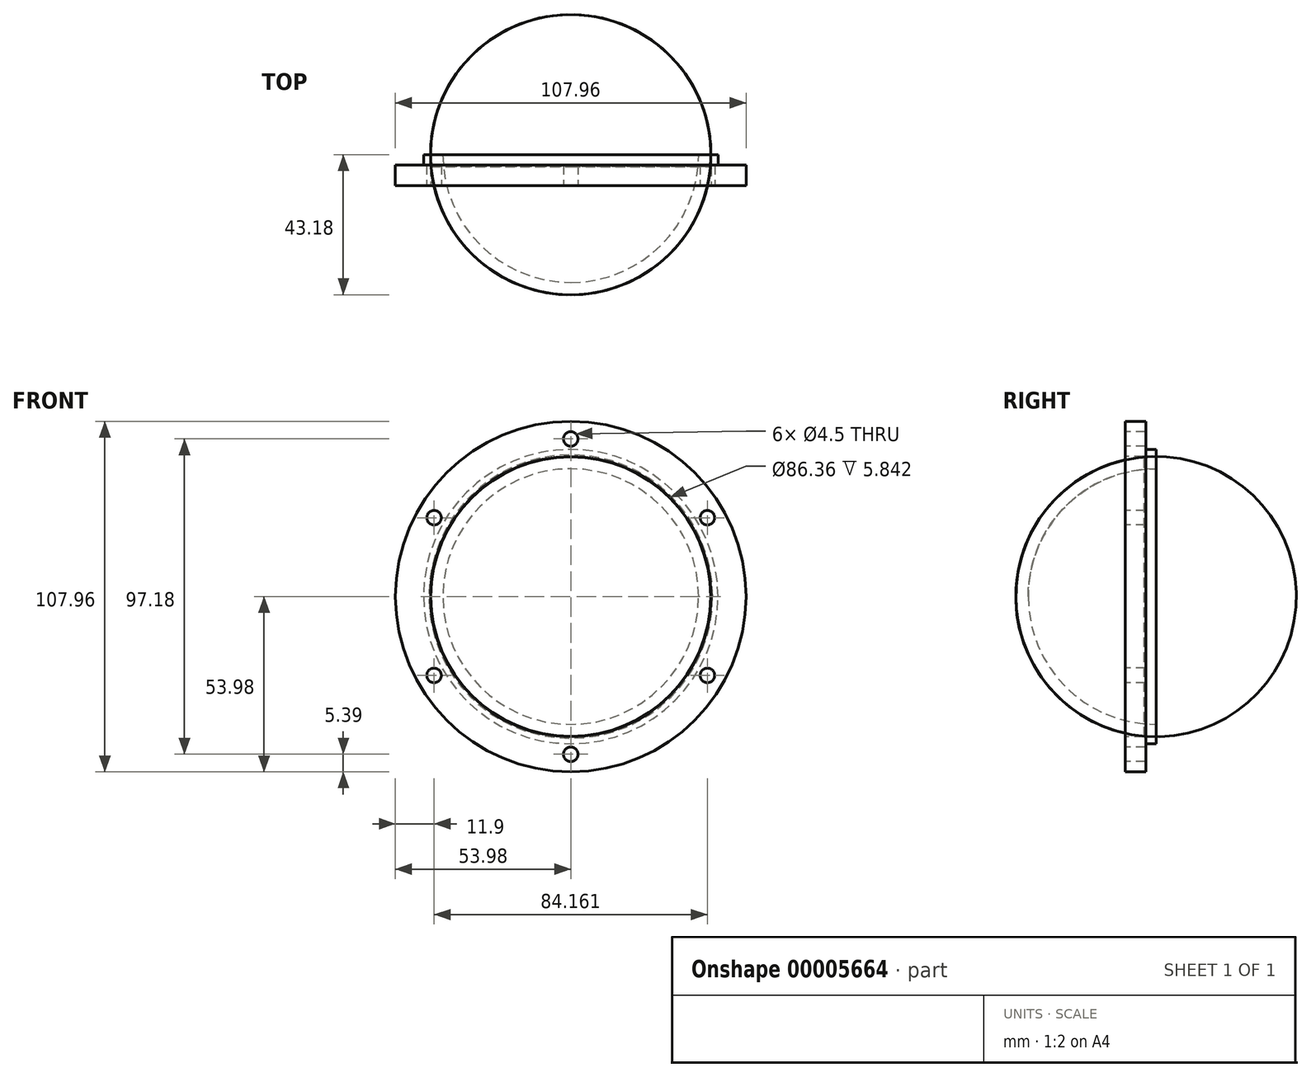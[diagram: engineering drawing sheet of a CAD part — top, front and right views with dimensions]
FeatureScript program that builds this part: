
annotation { "Feature Type Name" : "Feature", "Feature Type Description" : "" }
export const myFeature = defineFeature(function(context is Context, id is Id, definition is map)
    precondition{}
    {
        {
            var Q0;
            Q0=qCreatedBy(makeId("Right.planeOp"),FACE);
            var sketch = newSketch(context, id + "F0", { "sketchPlane" : qUnion([Q0])});
            skLineSegment(sketch, "E0", {"start": v(0, 0) * mm, "end": v(55.44, 0) * mm, "construction": true});
            skLineSegment(sketch, "E1", {"start": v(0, 43.18) * mm, "end": v(6.35, 43.18) * mm});
            skLineSegment(sketch, "E2", {"start": v(6.35, 43.18) * mm, "end": v(6.35, 43.18) * mm});
            skLineSegment(sketch, "E3", {"start": v(6.35, 43.18) * mm, "end": v(6.35, 53.97) * mm});
            skLineSegment(sketch, "E4", {"start": v(6.35, 53.97) * mm, "end": v(0, 53.97) * mm});
            skLineSegment(sketch, "E5", {"start": v(0, 53.97) * mm, "end": v(0, 43.18) * mm});
            skSolve(sketch);
        }
        {
            var Q0;
            Q0=makeQuery(id+"F0.imprint","IMPRINT",FACE,{"disambiguationData":[TD([[makeQuery(id+"F0.imprint","IMPRINT",EDGE,{"derivedFrom":sQuery(id+"F0.wireOp",EDGE,"E1")}),1.0]])]});
            var Q1;
            Q1=sQuery(id+"F0.wireOp",EDGE,"E0");
            revolve(context, id + "F1", {"entities" : qUnion([Q0]), "axis" : qUnion([Q1]), "revolveType" : RevolveType.FULL});
        }
        {
            var Q0;
            Q0=makeQuery(id+"F1.opRevolve","SWEPT_FACE",FACE,{"disambiguationData":[OSD([sQuery(id+"F0.wireOp",EDGE,"E5")])]});
            var sketch = newSketch(context, id + "F2", { "sketchPlane" : qUnion([Q0])});
            skCircle(sketch, "E6", {"center": v(0, 0) * mm, "radius": 48.6 * mm, "construction": true});
            skCircle(sketch, "E7", {"center": v(0, 48.6) * mm, "radius": 2.25 * mm});
            skCircle(sketch, "E8.1.0", {"center": v(-42.08, 24.3) * mm, "radius": 2.25 * mm});
            skCircle(sketch, "E8.2.0", {"center": v(-42.08, -24.3) * mm, "radius": 2.25 * mm});
            skCircle(sketch, "E8.3.0", {"center": v(0, -48.6) * mm, "radius": 2.25 * mm});
            skCircle(sketch, "E8.4.0", {"center": v(42.08, -24.3) * mm, "radius": 2.25 * mm});
            skCircle(sketch, "E8.5.0", {"center": v(42.08, 24.3) * mm, "radius": 2.25 * mm});
            skSolve(sketch);
        }
        {
            var Q0;
            Q0 = qSketchRegion(id + "F2", true);
            extrude(context, id + "F3", {"entities" : qUnion([Q0]), "operationType" : NewBodyOperationType.REMOVE, "endBound" : BoundingType.THROUGH_ALL, "oppositeDirection" : true, "depth" : 25.4 * mm, "offsetDistance" : 25.4 * mm});
        }
        {
            var Q0;
            Q0=makeQuery(id+"F1.opRevolve","SWEPT_EDGE",EDGE,{"disambiguationData":[OSD([sQuery(id+"F0.wireOp",EDGE,"E1"),sQuery(id+"F0.wireOp",EDGE,"E3")])]});
            chamfer(context, id + "F4", {"entities" : qUnion([Q0]), "width" : 0.5 * mm, "tangentPropagation" : true});
        }
        {
            var Q0;
            Q0=qCreatedBy(makeId("Right.planeOp"),FACE);
            var sketch = newSketch(context, id + "F5", { "sketchPlane" : qUnion([Q0])});
            skLineSegment(sketch, "E9", {"start": v(28.35, 0) * mm, "end": v(-39.19, 0) * mm, "construction": true});
            skArc(sketch, "E10", {"start": v(6.35, 43.06) * mm, "mid": v(-22.11, 29.39) * mm, "end": v(-33.65, 0) * mm});
            skArc(sketch, "E11", {"start": v(9.53, 39.37) * mm, "mid": v(-18.31, 27.84) * mm, "end": v(-29.84, 0) * mm});
            skLineSegment(sketch, "E12.top", {"start": v(9.53, 45.34) * mm, "end": v(6.35, 45.34) * mm});
            skLineSegment(sketch, "E12.left", {"start": v(9.53, 39.37) * mm, "end": v(9.53, 45.34) * mm});
            skLineSegment(sketch, "E12.right", {"start": v(6.35, 43.06) * mm, "end": v(6.35, 45.34) * mm});
            skLineSegment(sketch, "E13", {"start": v(-29.84, 0) * mm, "end": v(-33.65, 0) * mm});
            skSolve(sketch);
        }
        {
            var Q0;
            Q0 = qSketchRegion(id + "F5", true);
            var Q1;
            Q1=sQuery(id+"F5.wireOp",EDGE,"E9");
            revolve(context, id + "F6", {"entities" : qUnion([Q0]), "axis" : qUnion([Q1]), "revolveType" : RevolveType.FULL});
        }
    });
